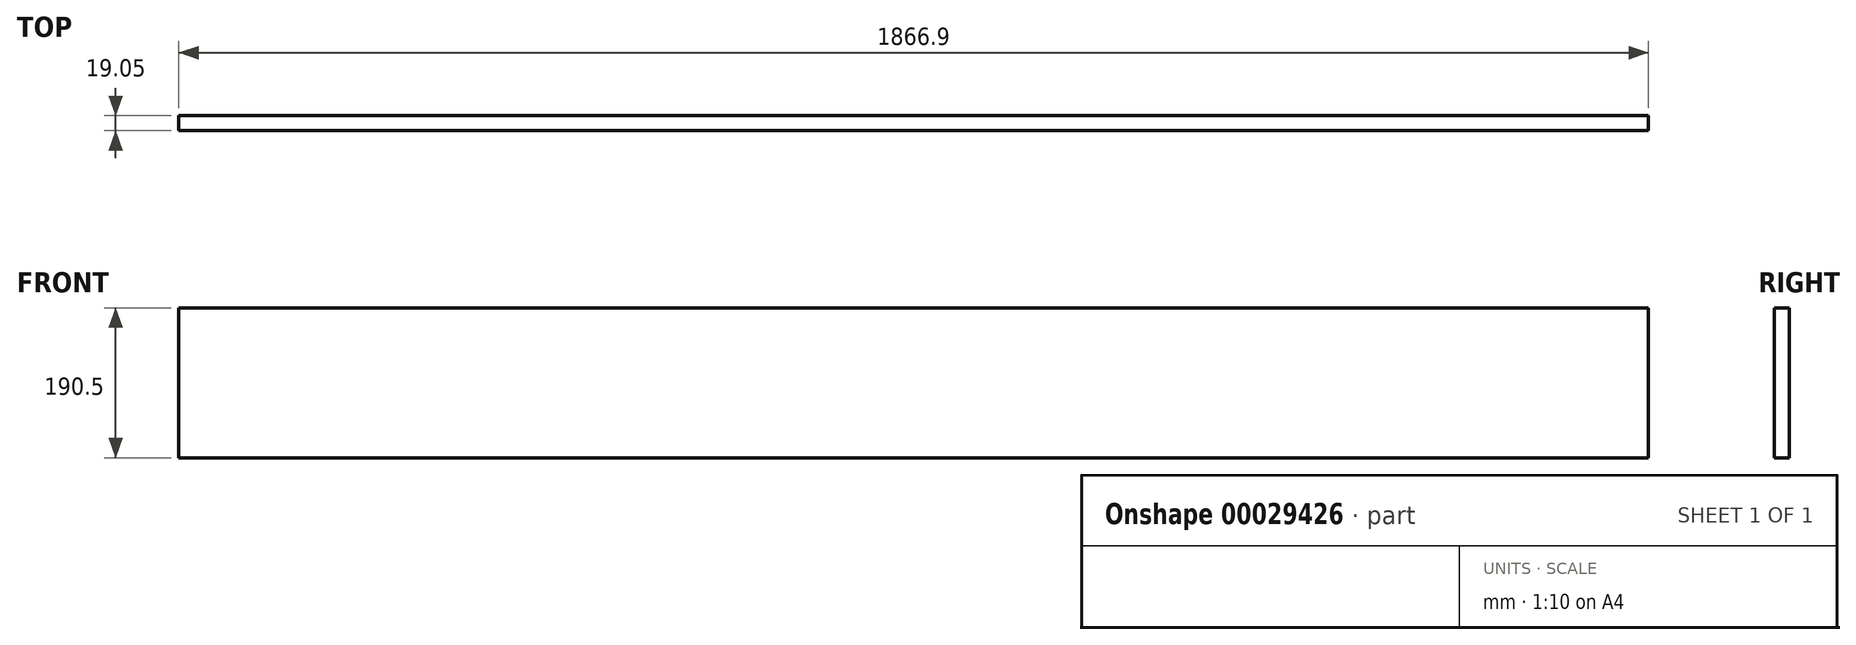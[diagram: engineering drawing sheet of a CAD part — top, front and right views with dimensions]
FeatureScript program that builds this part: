
annotation { "Feature Type Name" : "Feature", "Feature Type Description" : "" }
export const myFeature = defineFeature(function(context is Context, id is Id, definition is map)
    precondition{}
    {
        {
            var Q0;
            Q0=qCreatedBy(makeId("Front.planeOp"),FACE);
            var sketch = newSketch(context, id + "F0", { "sketchPlane" : qUnion([Q0])});
            skLineSegment(sketch, "E0.bottom", {"start": v(0, 0) * mm, "end": v(1866.9, 0) * mm});
            skLineSegment(sketch, "E0.top", {"start": v(0, 190.5) * mm, "end": v(1866.9, 190.5) * mm});
            skLineSegment(sketch, "E0.left", {"start": v(0, 0) * mm, "end": v(0, 190.5) * mm});
            skLineSegment(sketch, "E0.right", {"start": v(1866.9, 0) * mm, "end": v(1866.9, 190.5) * mm});
            skSolve(sketch);
        }
        {
            var Q0;
            Q0=makeQuery(id+"F0.imprint","IMPRINT",FACE,{"disambiguationData":[TD([[makeQuery(id+"F0.imprint","IMPRINT",EDGE,{"derivedFrom":sQuery(id+"F0.wireOp",EDGE,"E0.bottom")}),1.0]])]});
            extrude(context, id + "F1", {"entities" : qUnion([Q0]), "depth" : 19.05 * mm});
        }
    });
